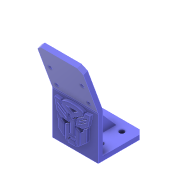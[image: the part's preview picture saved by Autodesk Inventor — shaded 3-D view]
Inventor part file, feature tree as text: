
AUTODESK INVENTOR PART (.ipt)
format: ipt  version: 2022 (Build 260153000, 153)  size: 588,800 bytes
history: native  units: mm
features: sketch x8, extrude x4, other x3, hole x2, rib x1, mirror x1, chamfer x1
ambient origin geometry x8: Origin, YZ Plane, XZ Plane, XY Plane, X Axis, Y Axis, Z Axis, Center Point
bodies: Solid1 (feature_tree)
feature tree (20):
  extrude  "Extrusion1"  Depth=30.0mm
  extrude  "Extrusion2"  Depth=21.0mm
  hole  "Mounting Holes"  [1 undecoded]
  rib  "Rib1"
  mirror  "Mirror1"
  other  "Bend Part1"
  hole  "Camera Mounting Holes"  [1 undecoded]
  chamfer  "Chamfer1"  Distance=3.0mm
  extrude  "Decepticon Logo"  Depth=13.5mm
  extrude  "Autobots Logo"  Depth=2.0mm
  sketch  "Sketch1"  dims[d0=30.0mm d1=30.0mm]
  sketch  "Sketch2"  dims[d2=3.0mm d3=0.0mm d4=21.0mm]
  sketch  "Sketch5"  dims[d5=13.0mm]
  sketch  "Sketch6"  dims[d7=2.4mm d8=6.0mm d9=4.0mm d10=2.0mm d11=90.0deg d12=6.0mm d13=0.0mm d15=30.0mm]
  sketch  "Sketch7"  dims[d16=30.0mm d17=3.0mm]
  sketch  "Sketch8"  dims[d18=3.0mm d19=3.0mm d20=0.0mm]
  other  "Image1"
  sketch  "Sketch10"  dims[d21=15.0mm d22=13.5mm]
  other  "Image2"
  sketch  "Sketch12"  dims[d23=7.0mm d24=3.4mm d25=6.0mm d26=4.0mm d27=2.0mm d28=90.0deg d29=6.0mm d30=0.0mm d31=22.0mm d35=1.0mm d36=2.0mm d37=0.0mm d38=0.0mm d39=1.0mm d40=1.0mm d41=27.0mm d42=32.0mm d43=3.0mm d44=2.0mm d45=45.0deg d71=2.0mm d72=0.0mm d157=2.0mm d158=0.0mm d162=3.0mm d163=3.490659mm d164=4.0mm d73=0.5mm d74=0.872665mm]
note: 2 required parameter values undecoded (feature->parameter linkage not recoverable at this tier; creation-order binding heuristic only, values carry confidence <= 0.55)
